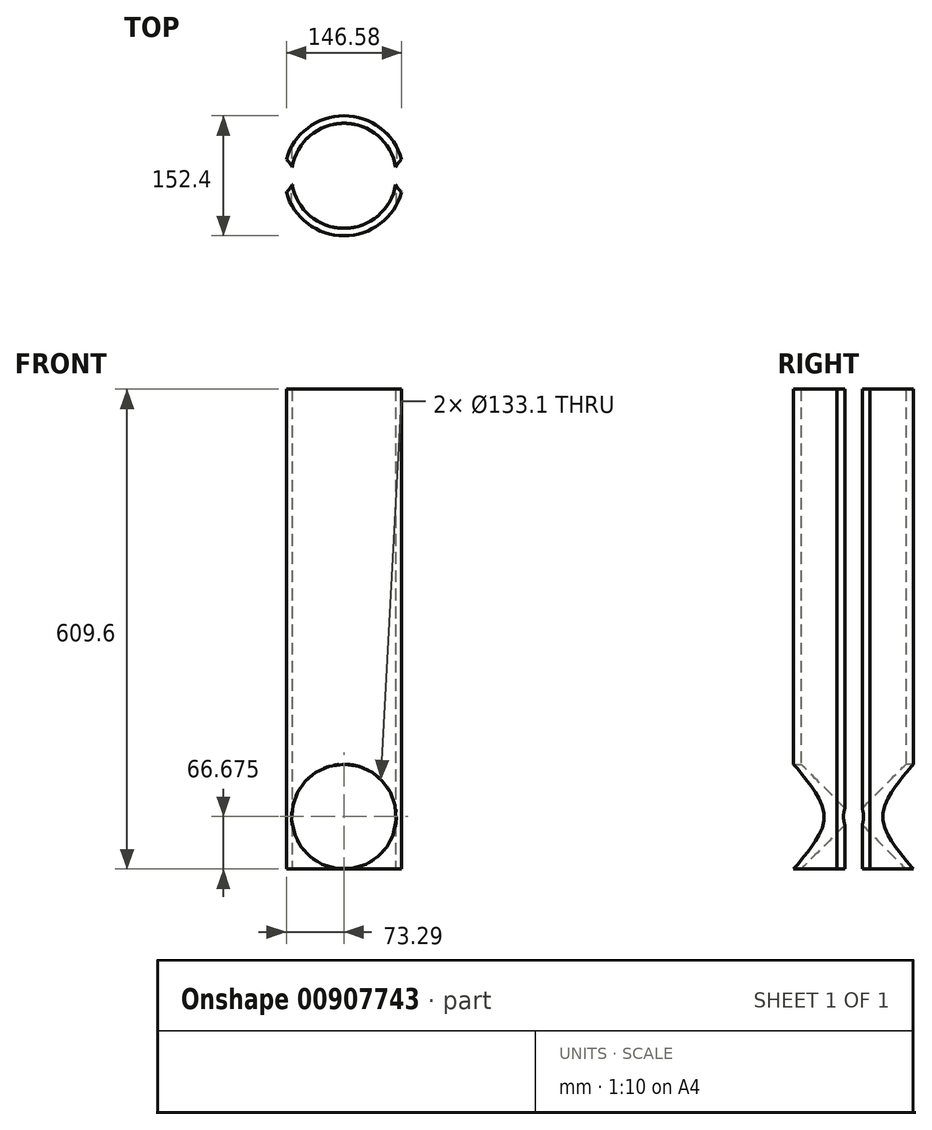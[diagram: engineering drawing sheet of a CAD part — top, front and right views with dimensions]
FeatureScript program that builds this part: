
annotation { "Feature Type Name" : "Feature", "Feature Type Description" : "" }
export const myFeature = defineFeature(function(context is Context, id is Id, definition is map)
    precondition{}
    {
        {
            var Q0;
            Q0=qCreatedBy(makeId("Top.planeOp"),FACE);
            var sketch = newSketch(context, id + "F0", { "sketchPlane" : qUnion([Q0])});
            skArc(sketch, "E0", {"start": v(-61.65, -25.4) * mm, "mid": v(0, -66.68) * mm, "end": v(61.65, -25.4) * mm});
            skArc(sketch, "E1", {"start": v(-71.84, -25.4) * mm, "mid": v(0, -76.2) * mm, "end": v(71.84, -25.4) * mm});
            skPoint(sketch, "E2.orphan", {"position": v(-58.57, -25.4) * mm});
            skPoint(sketch, "E3.orphan", {"position": v(-61.54, 25.4) * mm});
            skArc(sketch, "E4.trimOffspring", {"start": v(61.65, 25.4) * mm, "mid": v(0, 66.68) * mm, "end": v(-61.65, 25.4) * mm});
            skArc(sketch, "E5.trimOffspring", {"start": v(71.84, 25.4) * mm, "mid": v(0, 76.2) * mm, "end": v(-71.84, 25.4) * mm});
            skArc(sketch, "E6", {"start": v(-61.65, -25.4) * mm, "mid": v(-64.1, -18.35) * mm, "end": v(-65.75, -11.06) * mm});
            skArc(sketch, "E7.0", {"start": v(-65.75, 11.06) * mm, "mid": v(-68.95, 16.4) * mm, "end": v(-73.29, 20.87) * mm});
            skArc(sketch, "E8", {"start": v(-71.84, 25.4) * mm, "mid": v(-72.6, 23.15) * mm, "end": v(-73.29, 20.87) * mm});
            skArc(sketch, "E9", {"start": v(-71.84, -25.4) * mm, "mid": v(-72.6, -23.15) * mm, "end": v(-73.29, -20.87) * mm});
            skArc(sketch, "E10.trimOffspring", {"start": v(-65.75, 11.06) * mm, "mid": v(-64.1, 18.35) * mm, "end": v(-61.65, 25.4) * mm});
            skArc(sketch, "E11.trimOffspring", {"start": v(-73.29, -20.87) * mm, "mid": v(-68.95, -16.4) * mm, "end": v(-65.75, -11.06) * mm});
            skArc(sketch, "E12.MirrorCS", {"start": v(73.29, -20.87) * mm, "mid": v(68.95, -16.4) * mm, "end": v(65.75, -11.06) * mm});
            skArc(sketch, "E13.MirrorCS", {"start": v(61.65, -25.4) * mm, "mid": v(64.1, -18.35) * mm, "end": v(65.75, -11.06) * mm});
            skArc(sketch, "E14.MirrorCS", {"start": v(71.84, -25.4) * mm, "mid": v(72.6, -23.15) * mm, "end": v(73.29, -20.87) * mm});
            skArc(sketch, "E15.MirrorCS", {"start": v(65.75, 11.06) * mm, "mid": v(64.1, 18.35) * mm, "end": v(61.65, 25.4) * mm});
            skArc(sketch, "E16.MirrorCS", {"start": v(71.84, 25.4) * mm, "mid": v(72.6, 23.15) * mm, "end": v(73.29, 20.87) * mm});
            skArc(sketch, "E17.MirrorCS", {"start": v(65.75, 11.06) * mm, "mid": v(68.95, 16.4) * mm, "end": v(73.29, 20.87) * mm});
            skSolve(sketch);
        }
        {
            var Q0;
            Q0 = qSketchRegion(id + "F0", true);
            extrude(context, id + "F1", {"entities" : qUnion([Q0]), "depth" : 609.6 * mm, "offsetDistance" : 25.4 * mm});
        }
        {
            var Q0;
            Q0=qCreatedBy(makeId("Top.planeOp"),FACE);
            var sketch = newSketch(context, id + "F2", { "sketchPlane" : qUnion([Q0])});
            skCircle(sketch, "E18", {"center": v(0, 0) * mm, "radius": 76.2 * mm});
            skSolve(sketch);
        }
        {
            var Q0;
            Q0=qCreatedBy(makeId("Front.planeOp"),FACE);
            var sketch = newSketch(context, id + "F3", { "sketchPlane" : qUnion([Q0])});
            skCircle(sketch, "E19", {"center": v(0, 66.68) * mm, "radius": 66.55 * mm});
            skSolve(sketch);
        }
        {
            var Q0;
            Q0 = qSketchRegion(id + "F3", true);
            extrude(context, id + "F4", {"entities" : qUnion([Q0]), "operationType" : NewBodyOperationType.REMOVE, "oppositeDirection" : true, "depth" : 154.94 * mm, "offsetDistance" : 25.4 * mm});
        }
        {
            var Q0;
            Q0 = qSketchRegion(id + "F3", true);
            extrude(context, id + "F5", {"entities" : qUnion([Q0]), "operationType" : NewBodyOperationType.REMOVE, "depth" : 124.46 * mm, "offsetDistance" : 25.4 * mm});
        }
    });
